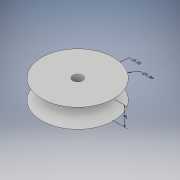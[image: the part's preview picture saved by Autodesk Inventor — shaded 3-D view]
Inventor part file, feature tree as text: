
AUTODESK INVENTOR PART (.ipt)
format: ipt  version: 2018 (Build 220112000, 112)  size: 122,880 bytes
history: native  units: in
note: dims shown in document units (in); Inventor stores cm internally (conversion verified against a paired STEP export)
features: other x4, extrude x3, sketch x3, chamfer x2
ambient origin geometry x8: Origin, YZ Plane, XZ Plane, XY Plane, X Axis, Y Axis, Z Axis, Center Point
bodies: Solid1 (feature_tree)
feature tree (12):
  other  "Annotations"
  extrude  "Extrusion1"  Depth=0.5in TaperAngle=0.0deg
  chamfer  "Chamfer1"  Distance=0.5in Angle=45.0deg
  extrude  "Extrusion2"  Depth=0.5in TaperAngle=0.0deg
  chamfer  "Chamfer2"  Distance=0.5in Angle=45.0deg
  extrude  "Extrusion4"  Depth=0.4in TaperAngle=0.0deg
  sketch  "Sketch1"  dims[d0=1.5in d1=0.2in d2=0.0in d3=0.5in d4=0.2in d5=45.0deg]
  sketch  "Sketch2"  dims[d6=1.5in d7=0.2in d8=0.0in d9=0.5in d10=0.2in d11=45.0deg]
  sketch  "Sketch5"  dims[d15=0.2in d16=0.4in d17=0.0in d18=1.6204in d19=1.5in d20=1.7728in d21=0.0611in d22=0.2321in d23=0.2in d24=0.4in]
  other  "Diameter Dimension 1"
  other  "Diameter Dimension 2"
  other  "Linear Dimension 1"
